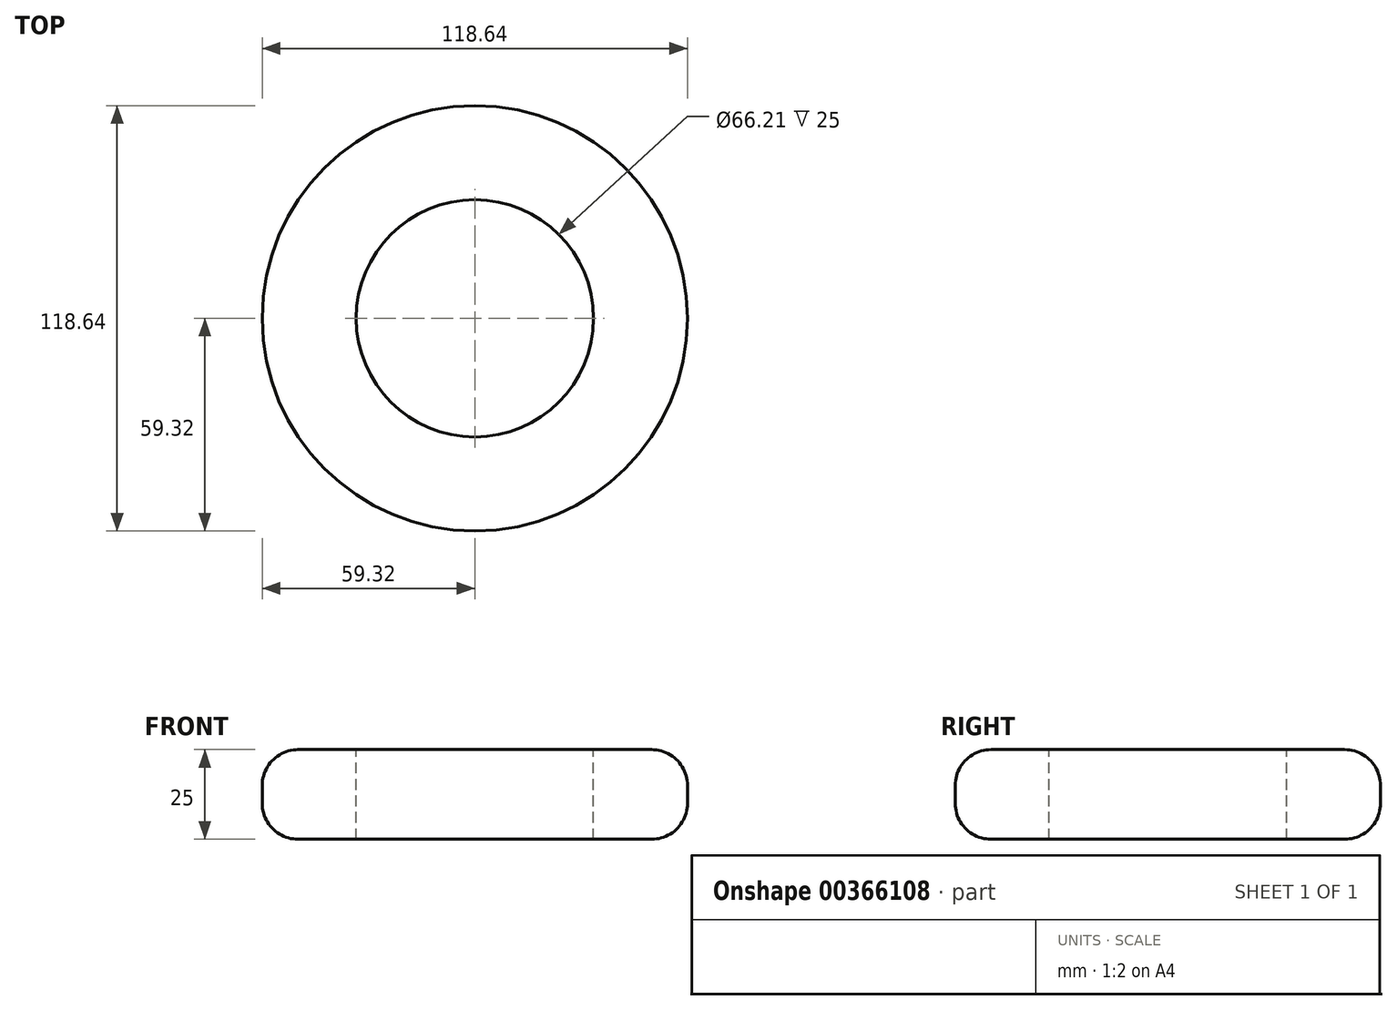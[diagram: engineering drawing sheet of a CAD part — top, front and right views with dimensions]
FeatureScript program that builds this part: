
annotation { "Feature Type Name" : "Feature", "Feature Type Description" : "" }
export const myFeature = defineFeature(function(context is Context, id is Id, definition is map)
    precondition{}
    {
        {
            var Q0;
            Q0=qCreatedBy(makeId("Top.planeOp"),FACE);
            var sketch = newSketch(context, id + "F0", { "sketchPlane" : qUnion([Q0])});
            skCircle(sketch, "E0", {"center": v(0, 0) * mm, "radius": 59.32 * mm});
            skSolve(sketch);
        }
        {
            var Q0;
            Q0=makeQuery(id+"F0.imprint","IMPRINT",FACE,{"disambiguationData":[TD([[makeQuery(id+"F0.imprint","IMPRINT",EDGE,{"derivedFrom":sQuery(id+"F0.wireOp",EDGE,"E0")}),1.0]])]});
            var Q1;
            Q1=makeQuery(id+"F0.imprint","IMPRINT",FACE,{"disambiguationData":[TD([[makeQuery(id+"F0.imprint","IMPRINT",EDGE,{"derivedFrom":sQuery(id+"F0.wireOp",EDGE,"E0")}),1.0]])]});
            extrude(context, id + "F1", {"entities" : qUnion([Q0, Q1]), "depth" : 25 * mm});
        }
        {
            var Q0;
            Q0=makeQuery(id+"F1.opExtrude","CAP_FACE",FACE,{"disambiguationData":[OSD([sQuery(id+"F0.wireOp",EDGE,"E0")])],"isStart":false});
            cPlane(context, id + "F2", {"entities" : qUnion([Q0]), "cplaneType" : CPlaneType.OFFSET, "offset" : 25 * mm, "width" : 150 * mm, "height" : 150 * mm});
        }
        {
            var Q0;
            Q0=qCreatedBy(id+"F2.planeOp",FACE);
            var sketch = newSketch(context, id + "F3", { "sketchPlane" : qUnion([Q0])});
            skCircle(sketch, "E1", {"center": v(0, 0) * mm, "radius": 33.1 * mm});
            skSolve(sketch);
        }
        {
            var Q0;
            Q0 = qSketchRegion(id + "F3", true);
            extrude(context, id + "F4", {"entities" : qUnion([Q0]), "operationType" : NewBodyOperationType.REMOVE, "oppositeDirection" : true, "depth" : 116.98 * mm});
        }
        {
            var Q0;
            Q0=makeQuery(id+"F1.opExtrude","CAP_EDGE",EDGE,{"disambiguationData":[OSD([sQuery(id+"F0.wireOp",EDGE,"E0")])],"isStart":true});
            var Q1;
            Q1=makeQuery(id+"F1.opExtrude","CAP_EDGE",EDGE,{"disambiguationData":[OSD([sQuery(id+"F0.wireOp",EDGE,"E0")])],"isStart":false});
            fillet(context, id + "F5", {"entities" : qUnion([Q0, Q1]), "radius" : 10 * mm, "tangentPropagation" : true, "allowEdgeOverflow" : false});
        }
    });
